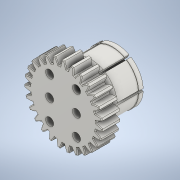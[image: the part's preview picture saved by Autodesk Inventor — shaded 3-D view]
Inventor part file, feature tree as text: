
AUTODESK INVENTOR PART (.ipt)
format: ipt  version: 2022 (Build 260153000, 153)  size: 1,009,152 bytes
history: native  units: mm (DEFAULTED — no unit token found)
features: sketch x9, extrude x7, fillet x5, plane x3, other x3, pattern_circular x3, revolve x1, projected_geometry x1
ambient origin geometry x8: Origin, YZ Plane, XZ Plane, XY Plane, X Axis, Y Axis, Z Axis, Center Point
bodies: Solid1 (feature_tree)
feature tree (32):
  extrude  "Extrusion1"  Depth=6.0mm TaperAngle=0.0deg
  plane  "Work Plane2"
  plane  "Work Plane8"
  plane  "Work Plane9"
  other  "Цилиндрическое зубчатое зацепление"
  extrude  "Выдавливание5"  Depth=10.0mm TaperAngle=0.0deg
  extrude  "Выдавливание7"  Depth=0.4mm
  extrude  "Выдавливание8"  Depth=0.4mm TaperAngle=0.0deg
  revolve  "Вращение1"
  extrude  "Выдавливание9"  TaperAngle=0.0deg  [1 undecoded]
  extrude  "Выдавливание11"  TaperAngle=0.0deg  [1 undecoded]
  fillet  "Сопряжение4"  Radius=40.825mm
  pattern_circular  "Круговой массив2"  [2 undecoded]
  fillet  "Сопряжение5"  [1 undecoded]
  fillet  "Сопряжение6"  Radius=4.0mm
  pattern_circular  "Круговой массив4"  [2 undecoded]
  extrude  "Выдавливание10"  Depth=0.4mm
  fillet  "Сопряжение2"  Radius=4.5mm
  pattern_circular  "Круговой массив1"  Count=3  [1 undecoded]
  fillet  "Сопряжение3"  Radius=8.0mm
  sketch  "Sketch1"  dims[d0=43.480844mm d1=6.0mm d2=0.0mm]
  sketch  "Sketch2"  dims[d3=40.5mm d4=10.0mm d5=0.0mm d16=40.825mm d17=0.0mm d34=1.163553mm d39=0.0mm d41=0.0mm d43=40.825mm d46=40.825mm d47=0.0mm d48=0.0mm d74=4.0mm d75=0.0mm d80=15.0mm d81=23.0mm d82=4.5mm d83=30.0mm d85=11.5mm d86=20.0mm d88=15.0mm d91=8.0mm d92=0.0mm d93=25.4mm d94=2.0mm d95=0.436332mm d96=60.0mm d98=360.0deg d100=20.0mm d101=0.0mm d102=2.5mm d103=0.3mm d104=12.0mm d105=90.0deg d106=21.0mm d107=20.0mm d108=0.0mm d109=0.5mm d110=10.0mm d111=0.0mm d112=1.0mm d113=80.0mm d114=360.0deg d116=0.5mm d117=0.3mm d118=0.872665mm d119=10.0mm d120=0.0mm d121=0.3mm d122=80.0mm d123=360.0deg d125=0.3mm d126=0.4mm d130=270.0mm d131=360.0deg]
  other  "Srf1"
  sketch  "Эскиз6"
  projected_geometry  "Спроецированная петля1"
  sketch  "Эскиз8"
  sketch  "Эскиз9"
  sketch  "Эскиз10"
  sketch  "Эскиз11"
  sketch  "Эскиз12"
  sketch  "Эскиз13"
  other  "Средний диаметр"
note: 8 required parameter values undecoded (feature->parameter linkage not recoverable at this tier; creation-order binding heuristic only, values carry confidence <= 0.55)
